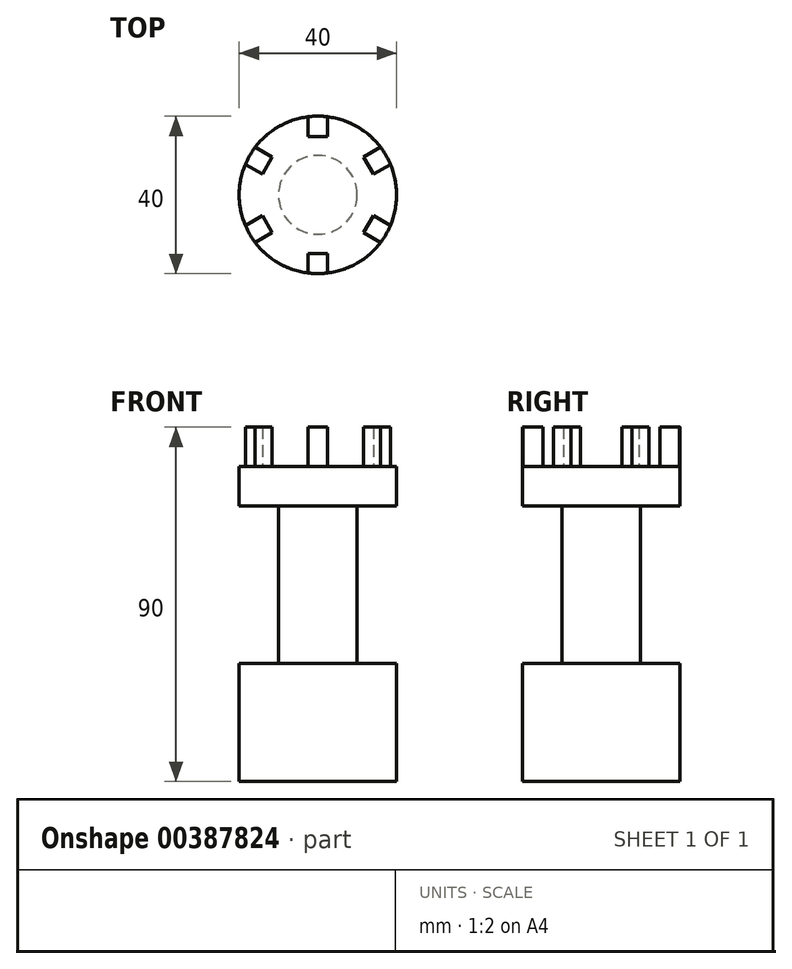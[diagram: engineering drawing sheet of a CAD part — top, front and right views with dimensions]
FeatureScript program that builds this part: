
annotation { "Feature Type Name" : "Feature", "Feature Type Description" : "" }
export const myFeature = defineFeature(function(context is Context, id is Id, definition is map)
    precondition{}
    {
        {
            var Q0;
            Q0=qCreatedBy(makeId("Front.planeOp"),FACE);
            var sketch = newSketch(context, id + "F0", { "sketchPlane" : qUnion([Q0])});
            skLineSegment(sketch, "E0", {"start": v(0, -30.5) * mm, "end": v(0, 49.5) * mm});
            skLineSegment(sketch, "E1", {"start": v(0, 49.5) * mm, "end": v(20, 49.5) * mm});
            skLineSegment(sketch, "E2", {"start": v(20, 49.5) * mm, "end": v(20, 39.5) * mm});
            skLineSegment(sketch, "E3", {"start": v(20, 39.5) * mm, "end": v(10, 39.5) * mm});
            skLineSegment(sketch, "E4", {"start": v(10, 39.5) * mm, "end": v(10, -0.5) * mm});
            skLineSegment(sketch, "E5", {"start": v(10, -0.5) * mm, "end": v(20, -0.5) * mm});
            skLineSegment(sketch, "E6", {"start": v(20, -0.5) * mm, "end": v(20, -30.5) * mm});
            skLineSegment(sketch, "E7", {"start": v(20, -30.5) * mm, "end": v(0, -30.5) * mm});
            skSolve(sketch);
        }
        {
            var Q0;
            Q0 = qSketchRegion(id + "F0", true);
            var Q1;
            Q1=sQuery(id+"F0.wireOp",EDGE,"E0");
            revolve(context, id + "F1", {"entities" : qUnion([Q0]), "axis" : qUnion([Q1]), "revolveType" : RevolveType.FULL});
        }
        {
            var Q0;
            Q0=makeQuery(id+"F1.opRevolve","SWEPT_FACE",FACE,{"disambiguationData":[OSD([sQuery(id+"F0.wireOp",EDGE,"E1")])]});
            var sketch = newSketch(context, id + "F2", { "sketchPlane" : qUnion([Q0])});
            skLineSegment(sketch, "E8", {"start": v(-2.5, 19.84) * mm, "end": v(-2.5, 14.84) * mm});
            skLineSegment(sketch, "E9", {"start": v(2.5, 14.84) * mm, "end": v(2.5, 19.84) * mm});
            skLineSegment(sketch, "E10", {"start": v(-2.5, 14.84) * mm, "end": v(2.5, 14.84) * mm});
            skArc(sketch, "E11", {"start": v(2.5, 19.84) * mm, "mid": v(0, 20) * mm, "end": v(-2.5, 19.84) * mm});
            skSolve(sketch);
        }
        {
            var Q0;
            Q0 = qSketchRegion(id + "F2", true);
            extrude(context, id + "F3", {"entities" : qUnion([Q0]), "operationType" : NewBodyOperationType.ADD, "depth" : 10 * mm});
        }
        {
            var Q0;
            Q0=makeQuery(id+"F1.opRevolve","SWEPT_BODY",BODY,{"disambiguationData":[OSD([sQuery(id+"F0.wireOp",EDGE,"E0"),sQuery(id+"F0.wireOp",EDGE,"E1"),sQuery(id+"F0.wireOp",EDGE,"E2"),sQuery(id+"F0.wireOp",EDGE,"E3"),sQuery(id+"F0.wireOp",EDGE,"E4"),sQuery(id+"F0.wireOp",EDGE,"E5"),sQuery(id+"F0.wireOp",EDGE,"E6"),sQuery(id+"F0.wireOp",EDGE,"E7")])]});
            var Q1;
            Q1=makeQuery(id+"F3.boolean.opBoolean","MERGE",FACE,{"derivedFrom":[makeQuery(id+"F1.opRevolve","SWEPT_FACE",FACE,{"disambiguationData":[OSD([sQuery(id+"F0.wireOp",EDGE,"E2")])]}),makeQuery(id+"F3.opExtrude","SWEPT_FACE",FACE,{"disambiguationData":[OSD([sQuery(id+"F2.wireOp",EDGE,"E11")])]})]});
            circularPattern(context, id + "F4", {"entities" : qUnion([Q0]), "axis" : qUnion([Q1]), "angle" : 360 * degree, "instanceCount" : 6, "equalSpace" : true});
        }
    });
